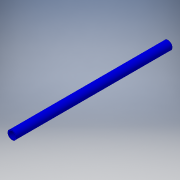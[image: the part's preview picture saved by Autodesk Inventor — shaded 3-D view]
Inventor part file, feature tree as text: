
AUTODESK INVENTOR PART (.ipt)
format: ipt  version: 2018.2 (Build 222227000, 227)  size: 105,472 bytes
history: native  units: in
note: dims shown in document units (in); Inventor stores cm internally (conversion verified against a paired STEP export)
features: extrude x1, sketch x1
ambient origin geometry x8: Origin, YZ Plane, XZ Plane, XY Plane, X Axis, Y Axis, Z Axis, Center Point
bodies: Solid1 (feature_tree)
feature tree (2):
  extrude  "Extrusion1"  Depth=24.0in
  sketch  "Sketch1"  dims[d0=1.315in d1=1.0in d2=24.0in d3=0.0in]
